# Revit family: Accessory-Flush_Actuator_Plate-KOHLER-PEBBLE-K-20341T
name_source: partatom
category: Specialty Equipment
revit_build: Autodesk Revit 2017 (Build: 20160225_1515(x64)
units: mm (PartAtom-declared; Revit-internal decimal feet)

## family parameters
Cut with Voids When Loaded = No
Host = Face
OmniClass Number = 23.31.25.00
OmniClass Title = Toilet and Bath Specialties
Part Type = Normal
Room Calculation Point = No
Round Connector Dimension = Use Diameter
Shared = No

## types (3) — shared parameters
ADA Compliant = No
Assembly Code = C1030200
Date Modified = 01/11/2021
Default Elevation = 42"
Height = 6 5/16"
Length = 9/16"
Manufacturer = KOHLER Co.
Master Format 2014 = 10 28 00
Master Format 2014 Name = Toilet, Bath, and Laundry Accessories
Material = Plastic
Product Documentation Link = https://files.kohler.com.cn
Product Name = PEBBLE
Product Page URL = https://www.kohler.com.cn
URL = http://www.kohler.com.cn
WaterSense Certified = No
Width = 8 7/8"

## per-type parameters (varying)
| type | Description | Finish | Model | Type |
| CP- Polished Chrome | PEBBLE concealed water tank panel | Kohler-Plastic-CP-Polished_Chrome | K-20341T-CP | 1 |
| Pneumatic, CP- Polished Chrome | PEBBLE Pneumatic hidden water tank panel | Kohler-Plastic-CP-Polished_Chrome | K-20341T-PNE-CP | 2 |
| Pneumatic, 0-White | PEBBLE Pneumatic hidden water tank panel | Kohler-Plastic-0-White | K-20341T-PNE-0 | 3 |

## geometry (parser evidence)
native form markers: Sweep x6
no freeform markers — native parametric forms only
